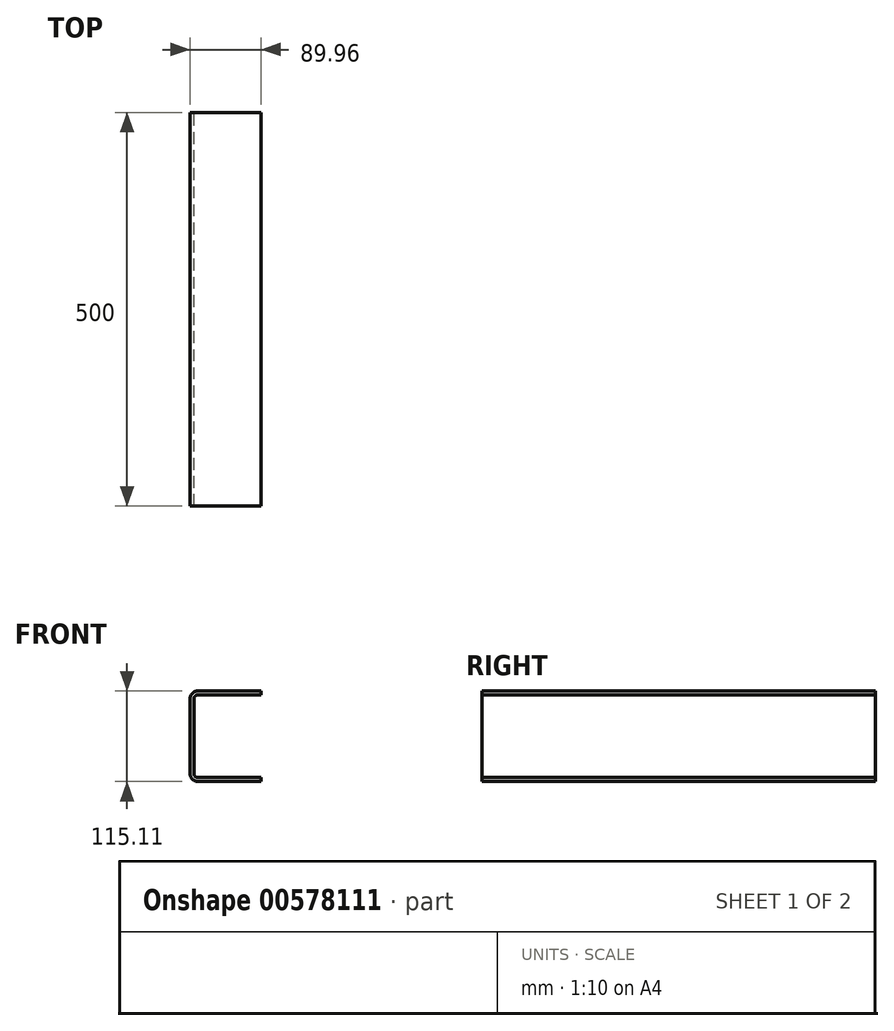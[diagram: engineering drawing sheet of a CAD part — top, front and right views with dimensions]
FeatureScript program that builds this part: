
annotation { "Feature Type Name" : "Feature", "Feature Type Description" : "" }
export const myFeature = defineFeature(function(context is Context, id is Id, definition is map)
    precondition{}
    {
        {
            var Q0;
            Q0=qCreatedBy(makeId("Front.planeOp"),FACE);
            var sketch = newSketch(context, id + "F0", { "sketchPlane" : qUnion([Q0])});
            skLineSegment(sketch, "E0", {"start": v(-55.13, 44.94) * mm, "end": v(-55.13, -50.17) * mm});
            skLineSegment(sketch, "E1", {"start": v(-45.13, -60.17) * mm, "end": v(34.83, -60.17) * mm});
            skLineSegment(sketch, "E2", {"start": v(-45.13, 54.94) * mm, "end": v(34.83, 54.94) * mm});
            skPoint(sketch, "E3.visualSharp", {"position": v(-55.13, 54.94) * mm});
            skArc(sketch, "E3.filletArc", {"start": v(-45.13, 54.94) * mm, "mid": v(-52.2, 52.01) * mm, "end": v(-55.13, 44.94) * mm});
            skPoint(sketch, "E4.visualSharp", {"position": v(-55.13, -60.17) * mm});
            skArc(sketch, "E4.filletArc", {"start": v(-55.13, -50.17) * mm, "mid": v(-52.2, -57.24) * mm, "end": v(-45.13, -60.17) * mm});
            skLineSegment(sketch, "E5.0", {"start": v(-45.13, 49.94) * mm, "end": v(34.83, 49.94) * mm});
            skLineSegment(sketch, "E5.1", {"start": v(-45.13, -55.17) * mm, "end": v(34.83, -55.17) * mm});
            skArc(sketch, "E5.2", {"start": v(-50.13, -50.17) * mm, "mid": v(-48.67, -53.7) * mm, "end": v(-45.13, -55.17) * mm});
            skLineSegment(sketch, "E5.3", {"start": v(-50.13, 44.94) * mm, "end": v(-50.13, -50.17) * mm});
            skArc(sketch, "E5.4", {"start": v(-45.13, 49.94) * mm, "mid": v(-48.67, 48.48) * mm, "end": v(-50.13, 44.94) * mm});
            skLineSegment(sketch, "E6", {"start": v(34.83, 54.94) * mm, "end": v(34.83, 49.94) * mm});
            skLineSegment(sketch, "E7", {"start": v(34.83, -55.17) * mm, "end": v(34.83, -60.17) * mm});
            skSolve(sketch);
        }
        {
            var Q0;
            Q0=makeQuery(id+"F0.imprint","IMPRINT",FACE,{"disambiguationData":[TD([[makeQuery(id+"F0.imprint","IMPRINT",EDGE,{"derivedFrom":sQuery(id+"F0.wireOp",EDGE,"E0")}),1.0]])]});
            extrude(context, id + "F1", {"entities" : qUnion([Q0]), "endBound" : BoundingType.SYMMETRIC, "depth" : 500 * mm, "offsetDistance" : 25 * mm});
        }
    });
